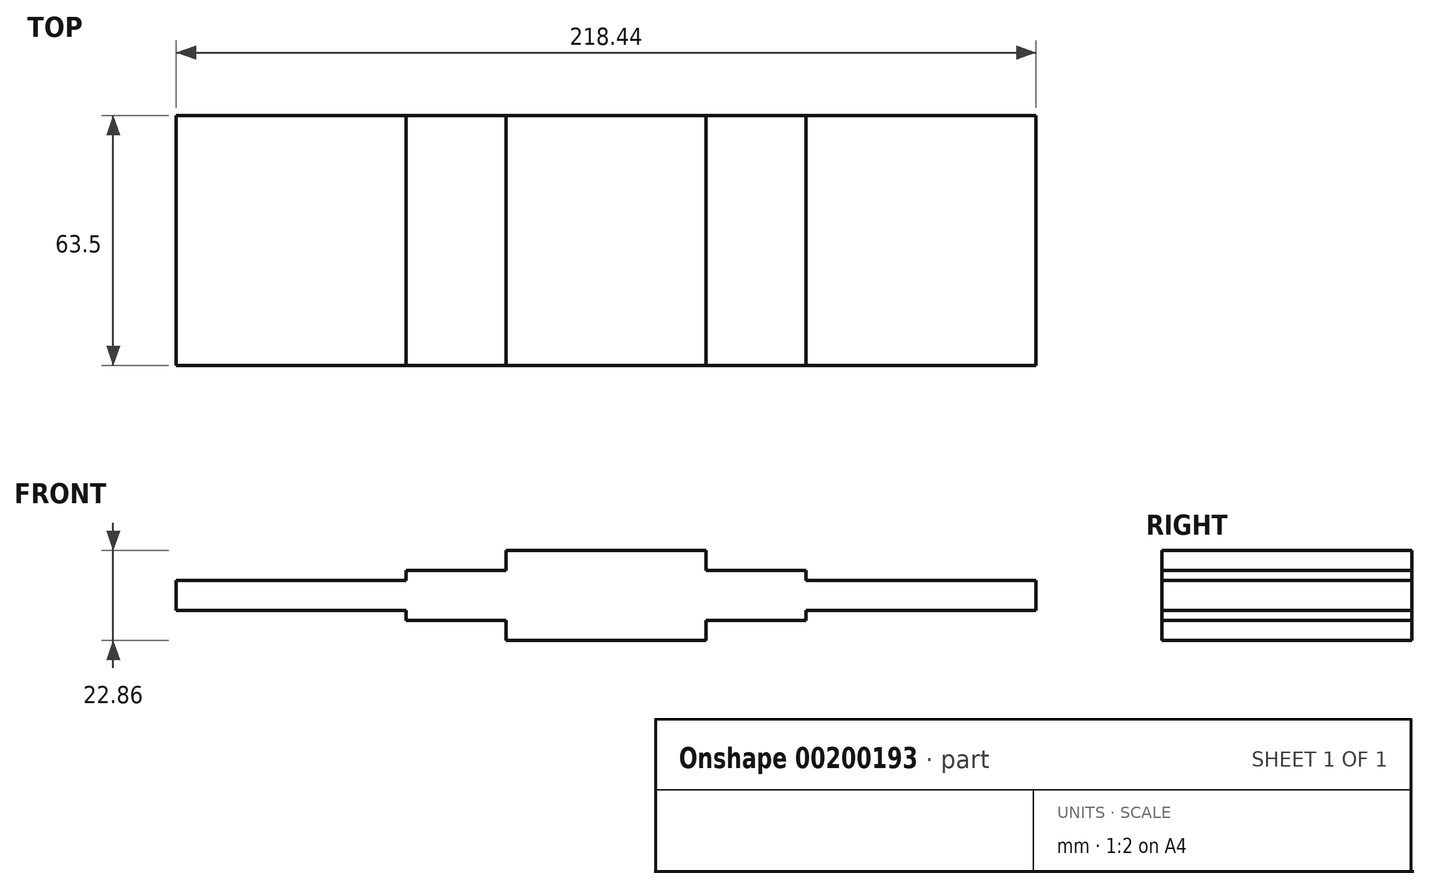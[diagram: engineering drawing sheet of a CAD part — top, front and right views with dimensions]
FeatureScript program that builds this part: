
annotation { "Feature Type Name" : "Feature", "Feature Type Description" : "" }
export const myFeature = defineFeature(function(context is Context, id is Id, definition is map)
    precondition{}
    {
        {
            var Q0;
            Q0=qCreatedBy(makeId("Front.planeOp"),FACE);
            var sketch = newSketch(context, id + "F0", { "sketchPlane" : qUnion([Q0])});
            skLineSegment(sketch, "E0", {"start": v(9.09, -17.78) * mm, "end": v(59.89, -17.78) * mm});
            skLineSegment(sketch, "E1", {"start": v(9.09, -17.78) * mm, "end": v(9.09, -12.7) * mm});
            skLineSegment(sketch, "E2", {"start": v(9.09, -12.7) * mm, "end": v(-16.31, -12.7) * mm});
            skLineSegment(sketch, "E3", {"start": v(-16.31, -12.7) * mm, "end": v(-16.31, -10.16) * mm});
            skLineSegment(sketch, "E4", {"start": v(-16.31, -10.16) * mm, "end": v(-74.73, -10.16) * mm});
            skLineSegment(sketch, "E5", {"start": v(-74.73, -10.16) * mm, "end": v(-74.73, -2.54) * mm});
            skLineSegment(sketch, "E6", {"start": v(-74.73, -2.54) * mm, "end": v(-16.31, -2.54) * mm});
            skLineSegment(sketch, "E7", {"start": v(-16.31, -2.54) * mm, "end": v(-16.31, 0) * mm});
            skLineSegment(sketch, "E8", {"start": v(-16.31, 0) * mm, "end": v(9.09, 0) * mm});
            skLineSegment(sketch, "E9", {"start": v(9.09, 0) * mm, "end": v(9.09, 5.08) * mm});
            skLineSegment(sketch, "E10", {"start": v(9.09, 5.08) * mm, "end": v(59.89, 5.08) * mm});
            skLineSegment(sketch, "E11", {"start": v(59.89, 5.08) * mm, "end": v(59.89, 0) * mm});
            skLineSegment(sketch, "E12", {"start": v(59.89, 0) * mm, "end": v(85.29, 0) * mm});
            skLineSegment(sketch, "E13", {"start": v(59.89, -17.78) * mm, "end": v(59.89, -12.7) * mm});
            skLineSegment(sketch, "E14", {"start": v(85.29, 0) * mm, "end": v(85.29, -2.54) * mm});
            skLineSegment(sketch, "E15", {"start": v(85.29, -2.54) * mm, "end": v(143.7, -2.54) * mm});
            skLineSegment(sketch, "E16", {"start": v(143.7, -2.54) * mm, "end": v(143.7, -10.16) * mm});
            skLineSegment(sketch, "E17", {"start": v(143.7, -10.16) * mm, "end": v(85.29, -10.16) * mm});
            skLineSegment(sketch, "E18", {"start": v(85.29, -10.16) * mm, "end": v(85.29, -12.7) * mm});
            skLineSegment(sketch, "E19", {"start": v(85.29, -12.7) * mm, "end": v(59.89, -12.7) * mm});
            skSolve(sketch);
        }
        {
            var Q0;
            Q0 = qSketchRegion(id + "F0", true);
            extrude(context, id + "F1", {"entities" : qUnion([Q0]), "depth" : 63.5 * mm});
        }
    });
